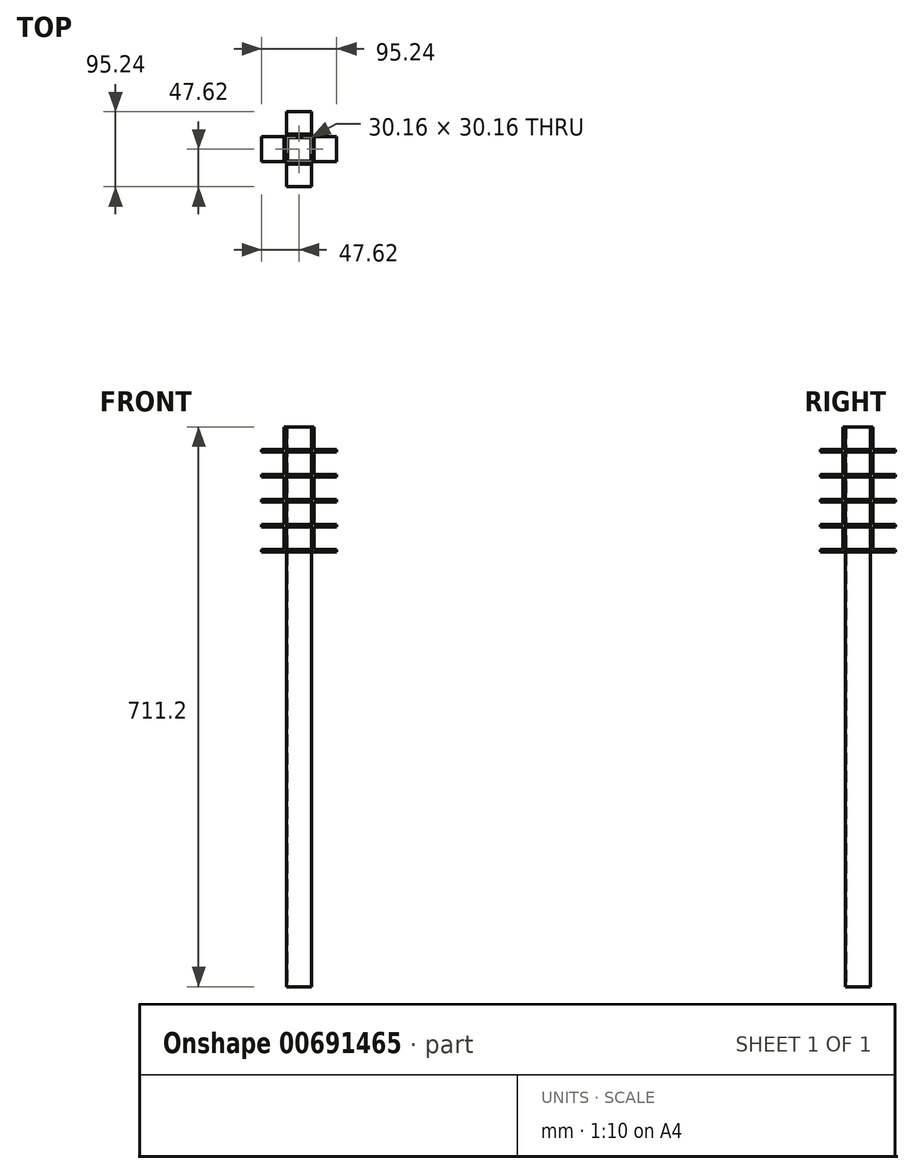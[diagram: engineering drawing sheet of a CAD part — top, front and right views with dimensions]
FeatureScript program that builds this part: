
annotation { "Feature Type Name" : "Feature", "Feature Type Description" : "" }
export const myFeature = defineFeature(function(context is Context, id is Id, definition is map)
    precondition{}
    {
        {
            var Q0;
            Q0=qCreatedBy(makeId("Top.planeOp"),FACE);
            var sketch = newSketch(context, id + "F0", { "sketchPlane" : qUnion([Q0])});
            skLineSegment(sketch, "E0.bottom", {"start": v(15.87, -15.88) * mm, "end": v(-15.88, -15.88) * mm});
            skLineSegment(sketch, "E0.top", {"start": v(15.88, 15.88) * mm, "end": v(-15.87, 15.88) * mm});
            skLineSegment(sketch, "E0.left", {"start": v(15.88, -15.88) * mm, "end": v(15.88, 15.88) * mm});
            skLineSegment(sketch, "E0.right", {"start": v(-15.88, -15.88) * mm, "end": v(-15.88, 15.87) * mm});
            skPoint(sketch, "E0.middle", {"position": v(0, 0) * mm});
            skLineSegment(sketch, "E1.bottom", {"start": v(15.08, -15.08) * mm, "end": v(-15.08, -15.08) * mm});
            skLineSegment(sketch, "E1.top", {"start": v(15.08, 15.08) * mm, "end": v(-15.08, 15.08) * mm});
            skLineSegment(sketch, "E1.left", {"start": v(15.08, -15.08) * mm, "end": v(15.08, 15.08) * mm});
            skLineSegment(sketch, "E1.right", {"start": v(-15.08, -15.08) * mm, "end": v(-15.08, 15.08) * mm});
            skSolve(sketch);
        }
        {
            var Q0;
            Q0 = qSketchRegion(id + "F0", true);
            extrude(context, id + "F1", {"entities" : qUnion([Q0]), "depth" : 711.2 * mm, "offsetDistance" : 25.4 * mm});
        }
        {
            var Q0;
            Q0=qCreatedBy(makeId("Top.planeOp"),FACE);
            var sketch = newSketch(context, id + "F2", { "sketchPlane" : qUnion([Q0])});
            skLineSegment(sketch, "E2.bottom", {"start": v(15.87, 15.87) * mm, "end": v(47.62, 15.87) * mm, "construction": true});
            skLineSegment(sketch, "E2.top", {"start": v(15.88, -15.88) * mm, "end": v(47.63, -15.87) * mm});
            skLineSegment(sketch, "E2.left", {"start": v(15.88, 15.87) * mm, "end": v(15.88, -15.88) * mm});
            skLineSegment(sketch, "E2.right", {"start": v(47.63, 15.87) * mm, "end": v(47.63, -15.87) * mm, "construction": true});
            skLineSegment(sketch, "E3.bottom", {"start": v(-15.88, 15.88) * mm, "end": v(15.88, 15.88) * mm});
            skLineSegment(sketch, "E3.top", {"start": v(-15.88, 47.63) * mm, "end": v(15.87, 47.63) * mm, "construction": true});
            skLineSegment(sketch, "E3.left", {"start": v(-15.88, 15.88) * mm, "end": v(-15.88, 47.63) * mm, "construction": true});
            skLineSegment(sketch, "E3.right", {"start": v(15.88, 15.88) * mm, "end": v(15.87, 47.63) * mm});
            skLineSegment(sketch, "E4.bottom", {"start": v(-15.88, -15.87) * mm, "end": v(-47.62, -15.87) * mm, "construction": true});
            skLineSegment(sketch, "E4.top", {"start": v(-15.88, 15.88) * mm, "end": v(-47.62, 15.88) * mm});
            skLineSegment(sketch, "E4.left", {"start": v(-15.87, -15.87) * mm, "end": v(-15.88, 15.88) * mm});
            skLineSegment(sketch, "E4.right", {"start": v(-47.62, -15.87) * mm, "end": v(-47.62, 15.88) * mm, "construction": true});
            skLineSegment(sketch, "E5.bottom", {"start": v(-15.88, -15.88) * mm, "end": v(15.88, -15.88) * mm});
            skLineSegment(sketch, "E5.top", {"start": v(-15.88, -47.62) * mm, "end": v(15.88, -47.62) * mm, "construction": true});
            skLineSegment(sketch, "E5.left", {"start": v(-15.88, -15.88) * mm, "end": v(-15.88, -47.62) * mm});
            skLineSegment(sketch, "E5.right", {"start": v(15.88, -15.87) * mm, "end": v(15.88, -47.62) * mm, "construction": true});
            skLineSegment(sketch, "E6", {"start": v(15.87, 15.87) * mm, "end": v(19.05, 15.87) * mm});
            skLineSegment(sketch, "E7", {"start": v(19.05, 15.88) * mm, "end": v(19.05, -12.7) * mm});
            skLineSegment(sketch, "E8", {"start": v(19.05, -12.7) * mm, "end": v(47.62, -12.7) * mm});
            skLineSegment(sketch, "E9", {"start": v(47.63, -12.7) * mm, "end": v(47.63, -15.87) * mm});
            skLineSegment(sketch, "E10", {"start": v(15.87, 47.63) * mm, "end": v(12.7, 47.63) * mm});
            skLineSegment(sketch, "E11", {"start": v(12.7, 47.63) * mm, "end": v(12.7, 19.05) * mm});
            skLineSegment(sketch, "E12", {"start": v(12.7, 19.05) * mm, "end": v(-15.87, 19.05) * mm});
            skLineSegment(sketch, "E13", {"start": v(-15.88, 19.05) * mm, "end": v(-15.88, 15.88) * mm});
            skLineSegment(sketch, "E14", {"start": v(-47.62, 15.88) * mm, "end": v(-47.62, 12.7) * mm});
            skLineSegment(sketch, "E15", {"start": v(-47.62, 12.7) * mm, "end": v(-19.05, 12.7) * mm});
            skLineSegment(sketch, "E16", {"start": v(-19.05, 12.7) * mm, "end": v(-19.05, -15.87) * mm});
            skLineSegment(sketch, "E17", {"start": v(-19.05, -15.87) * mm, "end": v(-15.88, -15.87) * mm});
            skLineSegment(sketch, "E18", {"start": v(-15.88, -47.62) * mm, "end": v(-12.7, -47.62) * mm});
            skLineSegment(sketch, "E19", {"start": v(-12.7, -47.63) * mm, "end": v(-12.7, -19.05) * mm});
            skLineSegment(sketch, "E20", {"start": v(-12.7, -19.05) * mm, "end": v(15.88, -19.05) * mm});
            skLineSegment(sketch, "E21", {"start": v(15.88, -19.05) * mm, "end": v(15.88, -15.88) * mm});
            skSolve(sketch);
        }
        {
            var Q0;
            Q0=qCreatedBy(makeId("Top.planeOp"),FACE);
            var sketch = newSketch(context, id + "F3", { "sketchPlane" : qUnion([Q0])});
            skLineSegment(sketch, "E22", {"start": v(-15.87, 19.05) * mm, "end": v(-15.87, 15.88) * mm});
            skLineSegment(sketch, "E23", {"start": v(-15.87, 15.88) * mm, "end": v(15.88, 15.88) * mm});
            skLineSegment(sketch, "E24", {"start": v(-15.87, 19.05) * mm, "end": v(12.7, 19.05) * mm});
            skLineSegment(sketch, "E25", {"start": v(12.7, 19.05) * mm, "end": v(32.9, 39.26) * mm});
            skLineSegment(sketch, "E26", {"start": v(32.9, 39.26) * mm, "end": v(35.13, 36.99) * mm});
            skLineSegment(sketch, "E27", {"start": v(35.13, 36.99) * mm, "end": v(15.87, 15.88) * mm});
            skLineSegment(sketch, "E28", {"start": v(15.88, 15.88) * mm, "end": v(19.05, 15.88) * mm});
            skLineSegment(sketch, "E29", {"start": v(19.05, 15.88) * mm, "end": v(19.05, -12.7) * mm});
            skLineSegment(sketch, "E30", {"start": v(19.05, -12.7) * mm, "end": v(39.12, -33.04) * mm});
            skLineSegment(sketch, "E31", {"start": v(39.12, -33.04) * mm, "end": v(36.86, -35.27) * mm});
            skLineSegment(sketch, "E32", {"start": v(36.86, -35.27) * mm, "end": v(15.87, -15.87) * mm});
            skLineSegment(sketch, "E33", {"start": v(15.88, -15.88) * mm, "end": v(15.88, 15.88) * mm});
            skLineSegment(sketch, "E34", {"start": v(15.88, -15.88) * mm, "end": v(-15.87, -15.88) * mm});
            skLineSegment(sketch, "E35", {"start": v(-15.87, -15.87) * mm, "end": v(-35.13, -36.99) * mm});
            skLineSegment(sketch, "E36", {"start": v(-35.13, -36.99) * mm, "end": v(-32.9, -39.26) * mm});
            skLineSegment(sketch, "E37", {"start": v(-32.9, -39.26) * mm, "end": v(-12.7, -19.05) * mm});
            skLineSegment(sketch, "E38", {"start": v(-12.7, -19.05) * mm, "end": v(15.88, -19.05) * mm});
            skLineSegment(sketch, "E39", {"start": v(15.88, -19.05) * mm, "end": v(15.88, -15.88) * mm});
            skLineSegment(sketch, "E40", {"start": v(-15.87, -15.88) * mm, "end": v(-15.87, 15.88) * mm});
            skLineSegment(sketch, "E41", {"start": v(-15.87, 15.87) * mm, "end": v(-36.99, 35.13) * mm});
            skLineSegment(sketch, "E42", {"start": v(-36.99, 35.13) * mm, "end": v(-39.26, 32.9) * mm});
            skLineSegment(sketch, "E43", {"start": v(-39.26, 32.9) * mm, "end": v(-19.05, 12.7) * mm});
            skLineSegment(sketch, "E44", {"start": v(-19.05, 12.7) * mm, "end": v(-19.05, -15.9) * mm});
            skLineSegment(sketch, "E45", {"start": v(-19.05, -15.9) * mm, "end": v(-15.87, -15.87) * mm});
            skSolve(sketch);
        }
        {
            var Q0;
            Q0=qCreatedBy(makeId("Top.planeOp"),FACE);
            var sketch = newSketch(context, id + "F4", { "sketchPlane" : qUnion([Q0])});
            skLineSegment(sketch, "E46.bottom", {"start": v(15.87, 15.88) * mm, "end": v(-15.88, 15.87) * mm});
            skLineSegment(sketch, "E46.top", {"start": v(15.87, 47.63) * mm, "end": v(-15.88, 47.62) * mm});
            skLineSegment(sketch, "E46.left", {"start": v(15.87, 15.88) * mm, "end": v(15.87, 47.62) * mm});
            skLineSegment(sketch, "E46.right", {"start": v(-15.88, 15.87) * mm, "end": v(-15.88, 47.62) * mm});
            skPoint(sketch, "E46.middle", {"position": v(0, 31.75) * mm});
            skLineSegment(sketch, "E47.bottom", {"start": v(47.62, -15.88) * mm, "end": v(15.88, -15.87) * mm});
            skLineSegment(sketch, "E47.top", {"start": v(47.62, 15.87) * mm, "end": v(15.88, 15.88) * mm});
            skLineSegment(sketch, "E47.left", {"start": v(47.62, -15.88) * mm, "end": v(47.62, 15.87) * mm});
            skLineSegment(sketch, "E47.right", {"start": v(15.88, -15.88) * mm, "end": v(15.87, 15.88) * mm});
            skPoint(sketch, "E47.middle", {"position": v(31.75, 0) * mm});
            skLineSegment(sketch, "E48.bottom", {"start": v(15.88, -47.62) * mm, "end": v(-15.88, -47.62) * mm});
            skLineSegment(sketch, "E48.top", {"start": v(15.87, -15.88) * mm, "end": v(-15.88, -15.87) * mm});
            skLineSegment(sketch, "E48.left", {"start": v(15.88, -47.62) * mm, "end": v(15.88, -15.88) * mm});
            skLineSegment(sketch, "E48.right", {"start": v(-15.88, -47.62) * mm, "end": v(-15.88, -15.87) * mm});
            skPoint(sketch, "E48.middle", {"position": v(0, -31.75) * mm});
            skLineSegment(sketch, "E49.bottom", {"start": v(-15.88, -15.88) * mm, "end": v(-47.62, -15.87) * mm});
            skLineSegment(sketch, "E49.top", {"start": v(-15.88, 15.87) * mm, "end": v(-47.63, 15.88) * mm});
            skLineSegment(sketch, "E49.left", {"start": v(-15.88, -15.88) * mm, "end": v(-15.88, 15.88) * mm});
            skLineSegment(sketch, "E49.right", {"start": v(-47.62, -15.87) * mm, "end": v(-47.63, 15.88) * mm});
            skPoint(sketch, "E49.middle", {"position": v(-31.75, 0) * mm});
            skSolve(sketch);
        }
        {
            var Q0;
            Q0=makeQuery(id+"F4.imprint","IMPRINT",FACE,{"disambiguationData":[TD([[makeQuery(id+"F4.imprint","IMPRINT",EDGE,{"derivedFrom":sQuery(id+"F4.wireOp",EDGE,"E47.bottom")}),-1.0]])]});
            var Q1;
            Q1=makeQuery(id+"F4.imprint","IMPRINT",FACE,{"disambiguationData":[TD([[makeQuery(id+"F4.imprint","IMPRINT",EDGE,{"derivedFrom":sQuery(id+"F4.wireOp",EDGE,"E49.bottom")}),-1.0]])]});
            var Q2;
            Q2=makeQuery(id+"F4.imprint","IMPRINT",FACE,{"disambiguationData":[TD([[makeQuery(id+"F4.imprint","IMPRINT",EDGE,{"derivedFrom":sQuery(id+"F4.wireOp",EDGE,"E46.bottom")}),-1.0]])]});
            var Q3;
            Q3=makeQuery(id+"F4.imprint","IMPRINT",FACE,{"disambiguationData":[TD([[makeQuery(id+"F4.imprint","IMPRINT",EDGE,{"derivedFrom":sQuery(id+"F4.wireOp",EDGE,"E48.bottom")}),-1.0]])]});
            extrude(context, id + "F5", {"entities" : qUnion([Q0, Q1, Q2, Q3]), "operationType" : NewBodyOperationType.ADD, "depth" : 711.2 * mm, "offsetDistance" : 25.4 * mm, "hasSecondDirection" : true, "secondDirectionOppositeDirection" : false, "secondDirectionDepth" : 552.45 * mm});
        }
        {
            var Q0;
            Q0=qCreatedBy(makeId("Front.planeOp"),FACE);
            var sketch = newSketch(context, id + "F6", { "sketchPlane" : qUnion([Q0])});
            skLineSegment(sketch, "E50.bottom", {"start": v(47.63, 650.88) * mm, "end": v(19.05, 650.88) * mm});
            skLineSegment(sketch, "E50.top", {"start": v(47.63, 679.45) * mm, "end": v(19.05, 679.45) * mm});
            skLineSegment(sketch, "E50.left", {"start": v(47.63, 650.88) * mm, "end": v(47.63, 679.45) * mm});
            skLineSegment(sketch, "E50.right", {"start": v(19.05, 650.88) * mm, "end": v(19.05, 679.45) * mm});
            skLineSegment(sketch, "E51.bottom", {"start": v(47.62, 711.2) * mm, "end": v(19.05, 711.2) * mm});
            skLineSegment(sketch, "E51.top", {"start": v(47.63, 682.63) * mm, "end": v(19.05, 682.63) * mm});
            skLineSegment(sketch, "E51.left", {"start": v(47.62, 711.2) * mm, "end": v(47.62, 682.63) * mm});
            skLineSegment(sketch, "E51.right", {"start": v(19.05, 711.2) * mm, "end": v(19.05, 682.63) * mm});
            skLineSegment(sketch, "E52", {"start": v(0, 0) * mm, "end": v(0, 861.82) * mm, "construction": true});
            skLineSegment(sketch, "E53.MirrorCS", {"start": v(-19.05, 711.2) * mm, "end": v(-19.05, 682.63) * mm});
            skLineSegment(sketch, "E54.MirrorCS", {"start": v(-47.62, 711.2) * mm, "end": v(-19.05, 711.2) * mm});
            skLineSegment(sketch, "E55.MirrorCS", {"start": v(-47.63, 682.63) * mm, "end": v(-19.05, 682.63) * mm});
            skLineSegment(sketch, "E56.MirrorCS", {"start": v(-47.62, 711.2) * mm, "end": v(-47.62, 682.63) * mm});
            skLineSegment(sketch, "E57.MirrorCS", {"start": v(-47.63, 650.88) * mm, "end": v(-47.63, 679.45) * mm});
            skLineSegment(sketch, "E58.MirrorCS", {"start": v(-47.63, 679.45) * mm, "end": v(-19.05, 679.45) * mm});
            skLineSegment(sketch, "E59.MirrorCS", {"start": v(-19.05, 650.88) * mm, "end": v(-19.05, 679.45) * mm});
            skLineSegment(sketch, "E60.MirrorCS", {"start": v(-47.63, 650.88) * mm, "end": v(-19.05, 650.88) * mm});
            skLineSegment(sketch, "E61.bottom", {"start": v(19.05, 647.7) * mm, "end": v(47.63, 647.7) * mm});
            skLineSegment(sketch, "E61.top", {"start": v(19.05, 619.12) * mm, "end": v(47.63, 619.12) * mm});
            skLineSegment(sketch, "E61.left", {"start": v(19.05, 647.7) * mm, "end": v(19.05, 619.12) * mm});
            skLineSegment(sketch, "E61.right", {"start": v(47.63, 647.7) * mm, "end": v(47.63, 619.12) * mm});
            skLineSegment(sketch, "E62.bottom", {"start": v(19.05, 615.95) * mm, "end": v(47.63, 615.95) * mm});
            skLineSegment(sketch, "E62.top", {"start": v(19.05, 587.38) * mm, "end": v(47.63, 587.38) * mm});
            skLineSegment(sketch, "E62.left", {"start": v(19.05, 615.95) * mm, "end": v(19.05, 587.38) * mm});
            skLineSegment(sketch, "E62.right", {"start": v(47.63, 615.95) * mm, "end": v(47.63, 587.38) * mm});
            skLineSegment(sketch, "E63.bottom", {"start": v(19.05, 584.2) * mm, "end": v(47.63, 584.2) * mm});
            skLineSegment(sketch, "E63.top", {"start": v(19.05, 555.62) * mm, "end": v(47.63, 555.62) * mm});
            skLineSegment(sketch, "E63.left", {"start": v(19.05, 584.2) * mm, "end": v(19.05, 555.62) * mm});
            skLineSegment(sketch, "E63.right", {"start": v(47.63, 584.2) * mm, "end": v(47.63, 555.62) * mm});
            skLineSegment(sketch, "E64.MirrorCS", {"start": v(-19.05, 647.7) * mm, "end": v(-19.05, 619.12) * mm});
            skLineSegment(sketch, "E65.MirrorCS", {"start": v(-47.63, 647.7) * mm, "end": v(-47.63, 619.12) * mm});
            skLineSegment(sketch, "E66.MirrorCS", {"start": v(-19.05, 647.7) * mm, "end": v(-47.63, 647.7) * mm});
            skLineSegment(sketch, "E67.MirrorCS", {"start": v(-19.05, 619.12) * mm, "end": v(-47.63, 619.12) * mm});
            skLineSegment(sketch, "E68.MirrorCS", {"start": v(-19.05, 615.95) * mm, "end": v(-47.63, 615.95) * mm});
            skLineSegment(sketch, "E69.MirrorCS", {"start": v(-47.63, 615.95) * mm, "end": v(-47.63, 587.38) * mm});
            skLineSegment(sketch, "E70.MirrorCS", {"start": v(-19.05, 615.95) * mm, "end": v(-19.05, 587.38) * mm});
            skLineSegment(sketch, "E71.MirrorCS", {"start": v(-19.05, 587.38) * mm, "end": v(-47.63, 587.38) * mm});
            skLineSegment(sketch, "E72.MirrorCS", {"start": v(-19.05, 584.2) * mm, "end": v(-47.63, 584.2) * mm});
            skLineSegment(sketch, "E73.MirrorCS", {"start": v(-19.05, 584.2) * mm, "end": v(-19.05, 555.62) * mm});
            skLineSegment(sketch, "E74.MirrorCS", {"start": v(-47.63, 584.2) * mm, "end": v(-47.63, 555.62) * mm});
            skLineSegment(sketch, "E75.MirrorCS", {"start": v(-19.05, 555.62) * mm, "end": v(-47.63, 555.62) * mm});
            skSolve(sketch);
        }
        {
            var Q0;
            Q0 = qSketchRegion(id + "F6", true);
            extrude(context, id + "F7", {"entities" : qUnion([Q0]), "operationType" : NewBodyOperationType.REMOVE, "oppositeDirection" : true, "depth" : 25.4 * mm, "offsetDistance" : 25.4 * mm, "hasSecondDirection" : true, "secondDirectionOppositeDirection" : false, "secondDirectionDepth" : 25.4 * mm});
        }
        {
            var Q0;
            Q0=qCreatedBy(makeId("Right.planeOp"),FACE);
            var sketch = newSketch(context, id + "F8", { "sketchPlane" : qUnion([Q0])});
            skLineSegment(sketch, "E76.bottom", {"start": v(47.62, 711.2) * mm, "end": v(19.05, 711.2) * mm});
            skLineSegment(sketch, "E76.top", {"start": v(47.63, 682.63) * mm, "end": v(19.05, 682.63) * mm});
            skLineSegment(sketch, "E76.left", {"start": v(47.62, 711.2) * mm, "end": v(47.63, 682.63) * mm});
            skLineSegment(sketch, "E76.right", {"start": v(19.05, 711.2) * mm, "end": v(19.05, 682.63) * mm});
            skLineSegment(sketch, "E77.bottom", {"start": v(47.62, 679.45) * mm, "end": v(19.05, 679.45) * mm});
            skLineSegment(sketch, "E77.top", {"start": v(47.63, 650.88) * mm, "end": v(19.05, 650.88) * mm});
            skLineSegment(sketch, "E77.left", {"start": v(47.62, 679.45) * mm, "end": v(47.63, 650.88) * mm});
            skLineSegment(sketch, "E77.right", {"start": v(19.05, 679.45) * mm, "end": v(19.05, 650.88) * mm});
            skLineSegment(sketch, "E78", {"start": v(0, 0) * mm, "end": v(0, 941.43) * mm, "construction": true});
            skLineSegment(sketch, "E79.MirrorCS", {"start": v(-19.05, 711.2) * mm, "end": v(-19.05, 682.63) * mm});
            skLineSegment(sketch, "E80.MirrorCS", {"start": v(-47.63, 650.88) * mm, "end": v(-19.05, 650.88) * mm});
            skLineSegment(sketch, "E81.MirrorCS", {"start": v(-47.62, 711.2) * mm, "end": v(-47.63, 682.63) * mm});
            skLineSegment(sketch, "E82.MirrorCS", {"start": v(-47.62, 711.2) * mm, "end": v(-19.05, 711.2) * mm});
            skLineSegment(sketch, "E83.MirrorCS", {"start": v(-47.63, 682.63) * mm, "end": v(-19.05, 682.63) * mm});
            skLineSegment(sketch, "E84.MirrorCS", {"start": v(-47.62, 679.45) * mm, "end": v(-19.05, 679.45) * mm});
            skLineSegment(sketch, "E85.MirrorCS", {"start": v(-19.05, 679.45) * mm, "end": v(-19.05, 650.88) * mm});
            skLineSegment(sketch, "E86.MirrorCS", {"start": v(-47.62, 679.45) * mm, "end": v(-47.63, 650.88) * mm});
            skLineSegment(sketch, "E87.bottom", {"start": v(19.05, 647.7) * mm, "end": v(47.63, 647.7) * mm});
            skLineSegment(sketch, "E87.top", {"start": v(19.05, 619.12) * mm, "end": v(47.63, 619.12) * mm});
            skLineSegment(sketch, "E87.left", {"start": v(19.05, 647.7) * mm, "end": v(19.05, 619.12) * mm});
            skLineSegment(sketch, "E87.right", {"start": v(47.63, 647.7) * mm, "end": v(47.63, 619.12) * mm});
            skLineSegment(sketch, "E88.bottom", {"start": v(19.05, 615.95) * mm, "end": v(47.63, 615.95) * mm});
            skLineSegment(sketch, "E88.top", {"start": v(19.05, 587.38) * mm, "end": v(47.63, 587.38) * mm});
            skLineSegment(sketch, "E88.left", {"start": v(19.05, 615.95) * mm, "end": v(19.05, 587.38) * mm});
            skLineSegment(sketch, "E88.right", {"start": v(47.63, 615.95) * mm, "end": v(47.63, 587.38) * mm});
            skLineSegment(sketch, "E89.bottom", {"start": v(19.05, 584.2) * mm, "end": v(47.63, 584.2) * mm});
            skLineSegment(sketch, "E89.top", {"start": v(19.05, 555.62) * mm, "end": v(47.63, 555.62) * mm});
            skLineSegment(sketch, "E89.left", {"start": v(19.05, 584.2) * mm, "end": v(19.05, 555.62) * mm});
            skLineSegment(sketch, "E89.right", {"start": v(47.63, 584.2) * mm, "end": v(47.63, 555.62) * mm});
            skLineSegment(sketch, "E90.MirrorCS", {"start": v(-19.05, 647.7) * mm, "end": v(-19.05, 619.12) * mm});
            skLineSegment(sketch, "E91.MirrorCS", {"start": v(-19.05, 615.95) * mm, "end": v(-19.05, 587.38) * mm});
            skLineSegment(sketch, "E92.MirrorCS", {"start": v(-19.05, 584.2) * mm, "end": v(-19.05, 555.62) * mm});
            skLineSegment(sketch, "E93.MirrorCS", {"start": v(-19.05, 584.2) * mm, "end": v(-47.63, 584.2) * mm});
            skLineSegment(sketch, "E94.MirrorCS", {"start": v(-19.05, 555.62) * mm, "end": v(-47.63, 555.62) * mm});
            skLineSegment(sketch, "E95.MirrorCS", {"start": v(-47.63, 584.2) * mm, "end": v(-47.63, 555.62) * mm});
            skLineSegment(sketch, "E96.MirrorCS", {"start": v(-19.05, 587.38) * mm, "end": v(-47.63, 587.38) * mm});
            skLineSegment(sketch, "E97.MirrorCS", {"start": v(-47.63, 615.95) * mm, "end": v(-47.63, 587.38) * mm});
            skLineSegment(sketch, "E98.MirrorCS", {"start": v(-19.05, 615.95) * mm, "end": v(-47.63, 615.95) * mm});
            skLineSegment(sketch, "E99.MirrorCS", {"start": v(-19.05, 619.12) * mm, "end": v(-47.63, 619.12) * mm});
            skLineSegment(sketch, "E100.MirrorCS", {"start": v(-47.63, 647.7) * mm, "end": v(-47.63, 619.12) * mm});
            skLineSegment(sketch, "E101.MirrorCS", {"start": v(-19.05, 647.7) * mm, "end": v(-47.63, 647.7) * mm});
            skSolve(sketch);
        }
        {
            var Q0;
            Q0 = qSketchRegion(id + "F8", true);
            extrude(context, id + "F9", {"entities" : qUnion([Q0]), "operationType" : NewBodyOperationType.REMOVE, "oppositeDirection" : true, "depth" : 25.4 * mm, "offsetDistance" : 25.4 * mm, "hasSecondDirection" : true, "secondDirectionOppositeDirection" : false, "secondDirectionDepth" : 25.4 * mm});
        }
        {
            var Q0;
            Q0=qCreatedBy(makeId("Top.planeOp"),FACE);
            var sketch = newSketch(context, id + "F10", { "sketchPlane" : qUnion([Q0])});
            skLineSegment(sketch, "E102.bottom", {"start": v(15.08, 15.08) * mm, "end": v(-15.08, 15.08) * mm});
            skLineSegment(sketch, "E102.top", {"start": v(15.08, -15.08) * mm, "end": v(-15.08, -15.08) * mm});
            skLineSegment(sketch, "E102.left", {"start": v(15.08, 15.08) * mm, "end": v(15.08, -15.08) * mm});
            skLineSegment(sketch, "E102.right", {"start": v(-15.08, 15.08) * mm, "end": v(-15.08, -15.08) * mm});
            skPoint(sketch, "E102.middle", {"position": v(0, 0) * mm});
            skSolve(sketch);
        }
        {
            var Q0;
            Q0 = qSketchRegion(id + "F10", true);
            extrude(context, id + "F11", {"entities" : qUnion([Q0]), "depth" : 711.2 * mm, "offsetDistance" : 25.4 * mm, "hasSecondDirection" : true, "secondDirectionOppositeDirection" : false, "secondDirectionDepth" : 552.45 * mm});
        }
        {
            var Q0;
            Q0=makeQuery(id+"F11.opExtrude","SWEPT_BODY",BODY,{"disambiguationData":[OSD([sQuery(id+"F10.wireOp",EDGE,"E102.bottom"),sQuery(id+"F10.wireOp",EDGE,"E102.top"),sQuery(id+"F10.wireOp",EDGE,"E102.left"),sQuery(id+"F10.wireOp",EDGE,"E102.right")])]});
            deleteBodies(context, id + "F12", {"entities" : qUnion([Q0])});
        }
    });
